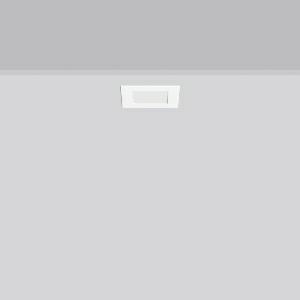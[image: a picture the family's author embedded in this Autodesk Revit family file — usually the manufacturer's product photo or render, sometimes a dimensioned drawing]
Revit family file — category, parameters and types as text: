
# Revit family: toledo_flat_square_e_672241_002_d60f
name_source: partatom
category: Lighting Fixtures
units: mm (PartAtom-declared; Revit-internal decimal feet)

## family parameters
Cut with Voids When Loaded = No
Host = Face
Light Source = No
Part Type = Normal
Room Calculation Point = No
Round Connector Dimension = Use Diameter
Shared = No

## types (1)
- TOLEDO FLAT square E (1 x LED Modul 830, 370 lm, 3000)
    Apparent Load = 5 VA
    CIE Flux Codes = 49 80 96 100 100
    Color Rendering = 80
    Color Temperature = 3000
    Default Elevation = 1800 mm
    Description = Series: TOLEDO FLAT square
Square recessed downlight. For escape route illumination. Housing: die-cast aluminium, powder-coated. Lightguide and diffuser made of non-yellowing plastic (PMMA). Diffuser opal matt plastic. Ceiling installation with spring system. Including separate LED converter with connecting cable 250 mm. Suitable for connection to central battery systems. External driver with simple plug-in locking system. 
Colour: white
Length: 110 mm
Width: 110 mm
Height: 3 mm
Cut-out length: 96 mm
Cut-out width: 96 mm
Recess height: 40 mm
Luminaire: recess height: 31-51 mm
Weight: 243 g
Operating mode: maintained power mode
Lamp: LED
Socket: without socket
Colour temperature: 3000K
Colour rendering index (CRI): 80
System power: 4.7 W
Rated luminous flux: 370 lm
Luminous flux, emergency: 370 lm
System power, emergency: 4.7 W
Control gear: Regulated power supply
Protection class: II
Type of protection: IP 54
    Height = 0 mm  [stored 0 ft]
    Lamp = 1 x LED Modul 830
    Lamp Light Flux = 370 lm
    Lamp count = 1
    Length = 110 mm
    Lifetime = 50000 h
    Luminous efficacy = 79 lm/W
    Manufacturer = RZB
    ModVariant = No
    Model = 672241.002
    Mounting Place = Ceiling
    Mounting Type = Recessed
    Number of Poles = 1
    OnlyDefault = Yes
    Power Factor = 1
    Product Name = TOLEDO FLAT square E
    Product group = Recessed downlights
    ProductGroupID = 402
    Protection Class = Protection class II
    Protection Degree = IP 40
    RLX_Detail_Level = 1
    RLX_Emergency_Light_Flux = 370 lm
    RLX_Emergency_Type = 3
    RLX_Emergency_Type_DB = Yes
    RlxData = <blob elided: 9609 chars, md5=205ac19a>
    Socket = socket
    Standby Power = 0 W
    System Light Flux = 370 lm
    System Power = 5 W
    Type Comments = Product without accessories
    Type Image = 901485.002.jpg
    URL = http://relux.com
    VarID = ---
    Voltage = 230 V
    Voltage Range = 220-240 V
    Weight = 0.00 kg
    Width = 110 mm

note: [stored X ft] marks values corroborated as IEEE doubles in the binary element streams (Revit-internal decimal feet)

## geometry (parser evidence)
native form markers: Sweep x11
no freeform markers — native parametric forms only
